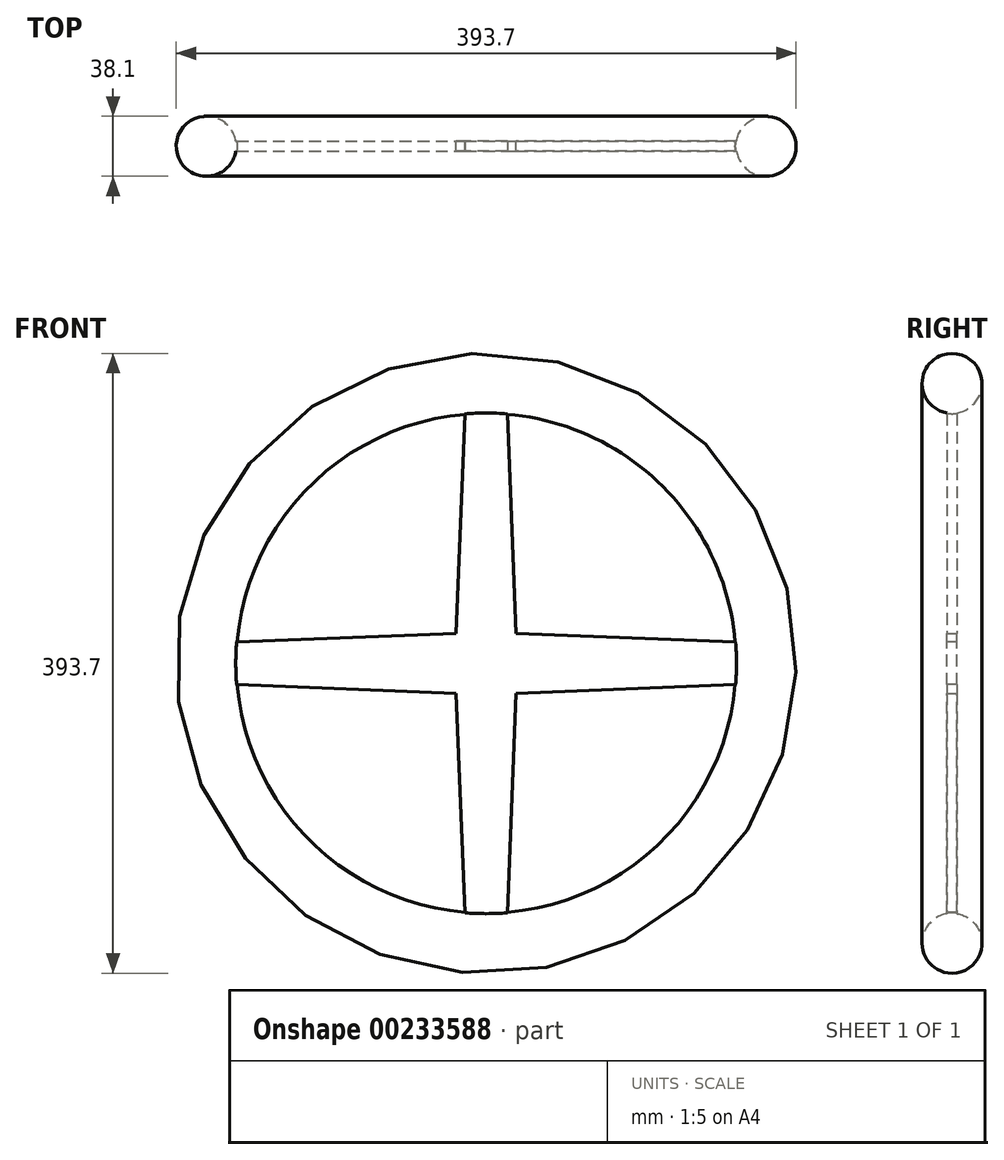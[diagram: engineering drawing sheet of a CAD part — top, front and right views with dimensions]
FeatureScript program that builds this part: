
annotation { "Feature Type Name" : "Feature", "Feature Type Description" : "" }
export const myFeature = defineFeature(function(context is Context, id is Id, definition is map)
    precondition{}
    {
        {
            var Q0;
            Q0=qCreatedBy(makeId("Front.planeOp"),FACE);
            var sketch = newSketch(context, id + "F0", { "sketchPlane" : qUnion([Q0])});
            skCircle(sketch, "E0", {"center": v(0, 0) * mm, "radius": 177.8 * mm});
            skLineSegment(sketch, "E1.0", {"start": v(-177.8, -19.05) * mm, "end": v(-19.05, -19.05) * mm});
            skLineSegment(sketch, "E2.0", {"start": v(-177.8, 19.05) * mm, "end": v(-176.78, 19.05) * mm});
            skLineSegment(sketch, "E3.0", {"start": v(-19.05, 177.8) * mm, "end": v(-19.05, 176.78) * mm});
            skLineSegment(sketch, "E4.0", {"start": v(19.05, 177.8) * mm, "end": v(19.05, 176.78) * mm});
            skLineSegment(sketch, "E5.trimOffspring", {"start": v(176.78, 19.05) * mm, "end": v(177.8, 19.05) * mm});
            skLineSegment(sketch, "E6.trimOffspring", {"start": v(176.78, -19.05) * mm, "end": v(177.8, -19.05) * mm});
            skLineSegment(sketch, "E7.trimOffspring", {"start": v(19.05, -176.78) * mm, "end": v(19.05, -177.8) * mm});
            skPoint(sketch, "E8.start.orphan", {"position": v(-177.8, 0) * mm});
            skLineSegment(sketch, "E9.bottom", {"start": v(-165.1, -12.7) * mm, "end": v(-190.5, -12.7) * mm});
            skLineSegment(sketch, "E9.top", {"start": v(-165.1, 12.7) * mm, "end": v(-190.5, 12.7) * mm});
            skLineSegment(sketch, "E9.left", {"start": v(-165.1, -12.7) * mm, "end": v(-165.1, 12.7) * mm});
            skLineSegment(sketch, "E9.right", {"start": v(-190.5, -12.7) * mm, "end": v(-190.5, 12.7) * mm});
            skLineSegment(sketch, "E10.bottom", {"start": v(12.7, -190.5) * mm, "end": v(-12.7, -190.5) * mm});
            skLineSegment(sketch, "E10.top", {"start": v(12.7, -165.1) * mm, "end": v(-12.7, -165.1) * mm});
            skLineSegment(sketch, "E10.left", {"start": v(12.7, -190.5) * mm, "end": v(12.7, -165.1) * mm});
            skLineSegment(sketch, "E10.right", {"start": v(-12.7, -190.5) * mm, "end": v(-12.7, -165.1) * mm});
            skPoint(sketch, "E10.middle", {"position": v(0, -177.8) * mm});
            skLineSegment(sketch, "E11.bottom", {"start": v(190.5, -12.7) * mm, "end": v(165.1, -12.7) * mm});
            skLineSegment(sketch, "E11.top", {"start": v(190.5, 12.7) * mm, "end": v(165.1, 12.7) * mm});
            skLineSegment(sketch, "E11.left", {"start": v(190.5, -12.7) * mm, "end": v(190.5, 12.7) * mm});
            skLineSegment(sketch, "E11.right", {"start": v(165.1, -12.7) * mm, "end": v(165.1, 12.7) * mm});
            skPoint(sketch, "E11.middle", {"position": v(177.8, 0) * mm});
            skLineSegment(sketch, "E12.bottom", {"start": v(12.7, 165.1) * mm, "end": v(-12.7, 165.1) * mm});
            skLineSegment(sketch, "E12.top", {"start": v(12.7, 190.5) * mm, "end": v(-12.7, 190.5) * mm});
            skLineSegment(sketch, "E12.left", {"start": v(12.7, 165.1) * mm, "end": v(12.7, 190.5) * mm});
            skLineSegment(sketch, "E12.right", {"start": v(-12.7, 165.1) * mm, "end": v(-12.7, 190.5) * mm});
            skPoint(sketch, "E12.middle", {"position": v(0, 177.8) * mm});
            skLineSegment(sketch, "E13", {"start": v(-177.35, 12.7) * mm, "end": v(-19.05, 19.05) * mm});
            skLineSegment(sketch, "E14", {"start": v(-177.8, -12.7) * mm, "end": v(-19.05, -19.05) * mm});
            skLineSegment(sketch, "E15", {"start": v(12.7, 177.8) * mm, "end": v(19.05, 19.05) * mm});
            skLineSegment(sketch, "E16", {"start": v(-12.7, 177.8) * mm, "end": v(-19.05, 19.05) * mm});
            skLineSegment(sketch, "E17", {"start": v(19.05, 19.05) * mm, "end": v(177.35, 12.7) * mm});
            skLineSegment(sketch, "E18", {"start": v(177.8, -12.7) * mm, "end": v(19.05, -19.05) * mm});
            skLineSegment(sketch, "E19", {"start": v(-19.05, -19.05) * mm, "end": v(-12.7, -177.35) * mm});
            skPoint(sketch, "E19.endSnap0", {"position": v(-12.7, -177.8) * mm});
            skLineSegment(sketch, "E20", {"start": v(12.7, -177.8) * mm, "end": v(19.05, -19.05) * mm});
            skLineSegment(sketch, "E21.trimOffspring", {"start": v(-19.05, -176.78) * mm, "end": v(-19.05, -177.8) * mm});
            skLineSegment(sketch, "E22.trimOffspring", {"start": v(-19.05, 19.05) * mm, "end": v(-19.05, -19.05) * mm});
            skSolve(sketch);
        }
        {
            var Q0;
            Q0=qCreatedBy(makeId("Right.planeOp"),FACE);
            var sketch = newSketch(context, id + "F1", { "sketchPlane" : qUnion([Q0])});
            skCircle(sketch, "E23", {"center": v(0, 177.8) * mm, "radius": 19.05 * mm});
            skSolve(sketch);
        }
        {
            var Q0;
            Q0=makeQuery(id+"F1.imprint","IMPRINT",FACE,{"disambiguationData":[TD([[makeQuery(id+"F1.imprint","IMPRINT",EDGE,{"derivedFrom":sQuery(id+"F1.wireOp",EDGE,"E23")}),1.0]])]});
            var Q1;
            Q1=sQuery(id+"F0.wireOp",EDGE,"E0");
            revolve(context, id + "F2", {"entities" : qUnion([Q0]), "axis" : qUnion([Q1]), "revolveType" : RevolveType.FULL});
        }
        {
            var Q0;
            {var subQ0=sQuery(id+"F0.wireOp",EDGE,"E9.left");Q0=makeQuery(id+"F0.imprint","IMPRINT",FACE,{"disambiguationData":[TD([[makeQuery(id+"F0.imprint","IMPRINT",EDGE,{"derivedFrom":subQ0}),-1.0]])]});}
            var Q1;
            {var subQ7=sQuery(id+"F0.wireOp",EDGE,"E10.top");Q1=makeQuery(id+"F0.imprint","IMPRINT",FACE,{"disambiguationData":[TD([[makeQuery(id+"F0.imprint","IMPRINT",EDGE,{"derivedFrom":subQ7}),-1.0]])]});}
            extrude(context, id + "F3", {"entities" : qUnion([Q0, Q1]), "operationType" : NewBodyOperationType.ADD, "endBound" : BoundingType.SYMMETRIC, "depth" : 6.35 * mm});
        }
    });
